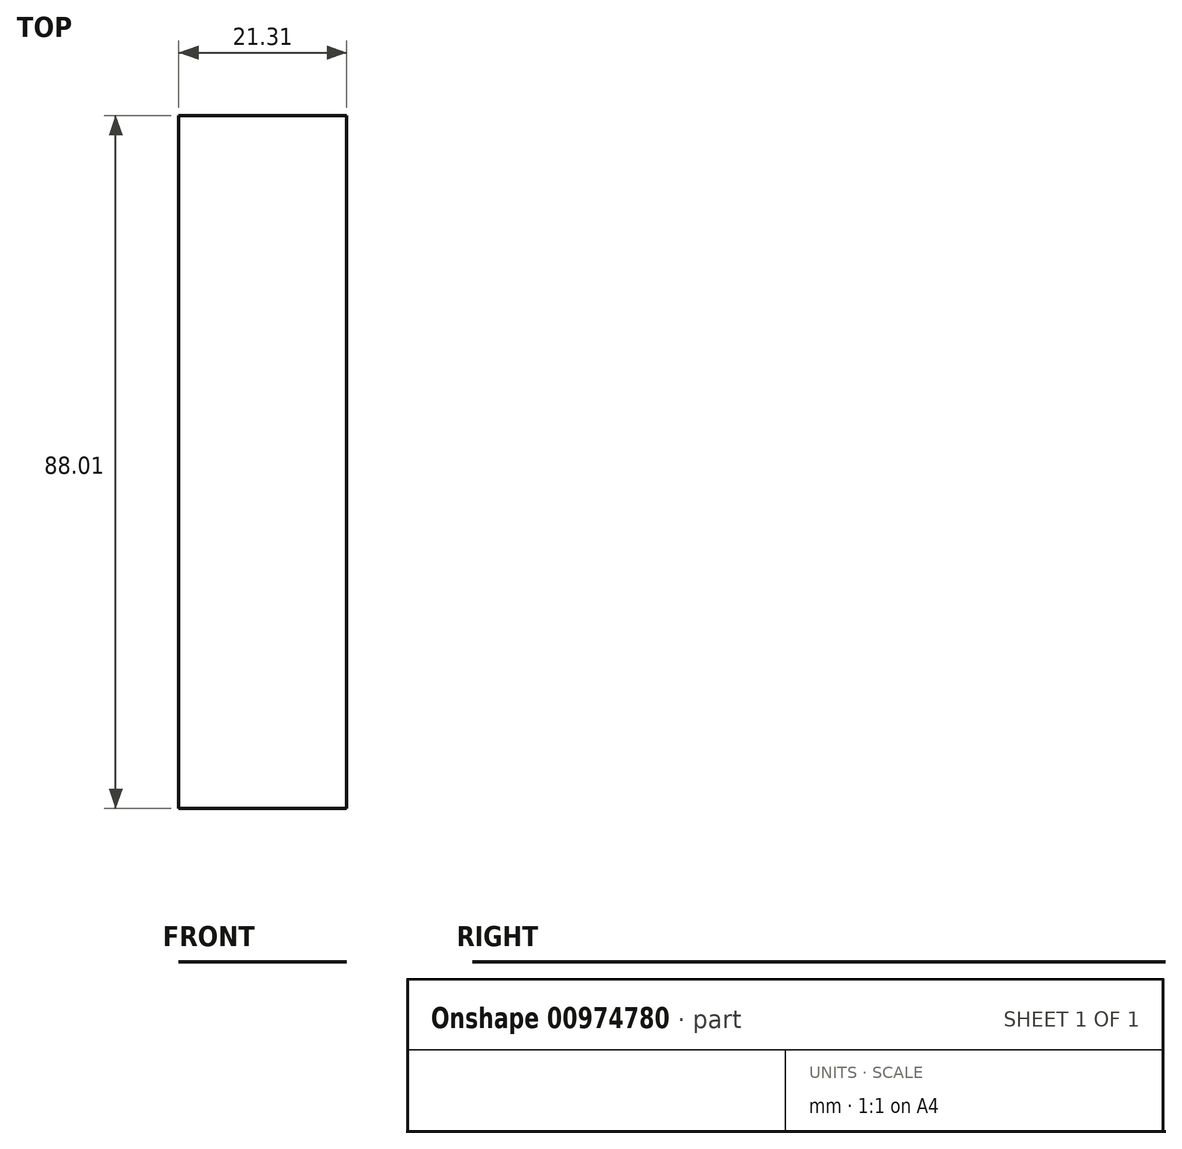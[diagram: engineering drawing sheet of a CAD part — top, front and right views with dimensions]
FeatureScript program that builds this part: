
annotation { "Feature Type Name" : "Feature", "Feature Type Description" : "" }
export const myFeature = defineFeature(function(context is Context, id is Id, definition is map)
    precondition{}
    {
        {
            var Q0;
            Q0=qCreatedBy(makeId("Front.planeOp"),FACE);
            var sketch = newSketch(context, id + "F0", { "sketchPlane" : qUnion([Q0])});
            skLineSegment(sketch, "E0.bottom", {"start": v(7.64, 14.87) * mm, "end": v(-13.67, 14.87) * mm});
            skLineSegment(sketch, "E0.top", {"start": v(7.64, -3.57) * mm, "end": v(-13.67, -3.57) * mm});
            skLineSegment(sketch, "E0.left", {"start": v(7.64, 14.87) * mm, "end": v(7.64, -3.57) * mm});
            skLineSegment(sketch, "E0.right", {"start": v(-13.67, 14.87) * mm, "end": v(-13.67, -3.57) * mm});
            skLineSegment(sketch, "E1.bottom", {"start": v(6.92, -2.4) * mm, "end": v(41.34, -2.4) * mm});
            skLineSegment(sketch, "E1.top", {"start": v(6.92, -26.14) * mm, "end": v(41.34, -26.14) * mm});
            skLineSegment(sketch, "E1.left", {"start": v(6.92, -2.4) * mm, "end": v(6.92, -26.14) * mm});
            skLineSegment(sketch, "E1.right", {"start": v(41.34, -2.4) * mm, "end": v(41.34, -26.14) * mm});
            skSolve(sketch);
        }
        {
            var Q0;
            Q0 = qSketchRegion(id + "F0", true);
            var Q1;
            Q1=sQuery(id+"F0.wireOp",EDGE,"E0.bottom");
            extrude(context, id + "F1", {"entities" : qUnion([Q0]), "bodyType" : ToolBodyType.SURFACE, "surfaceEntities" : qUnion([Q1]), "depth" : 88 * mm, "offsetDistance" : 25.4 * mm});
        }
    });
